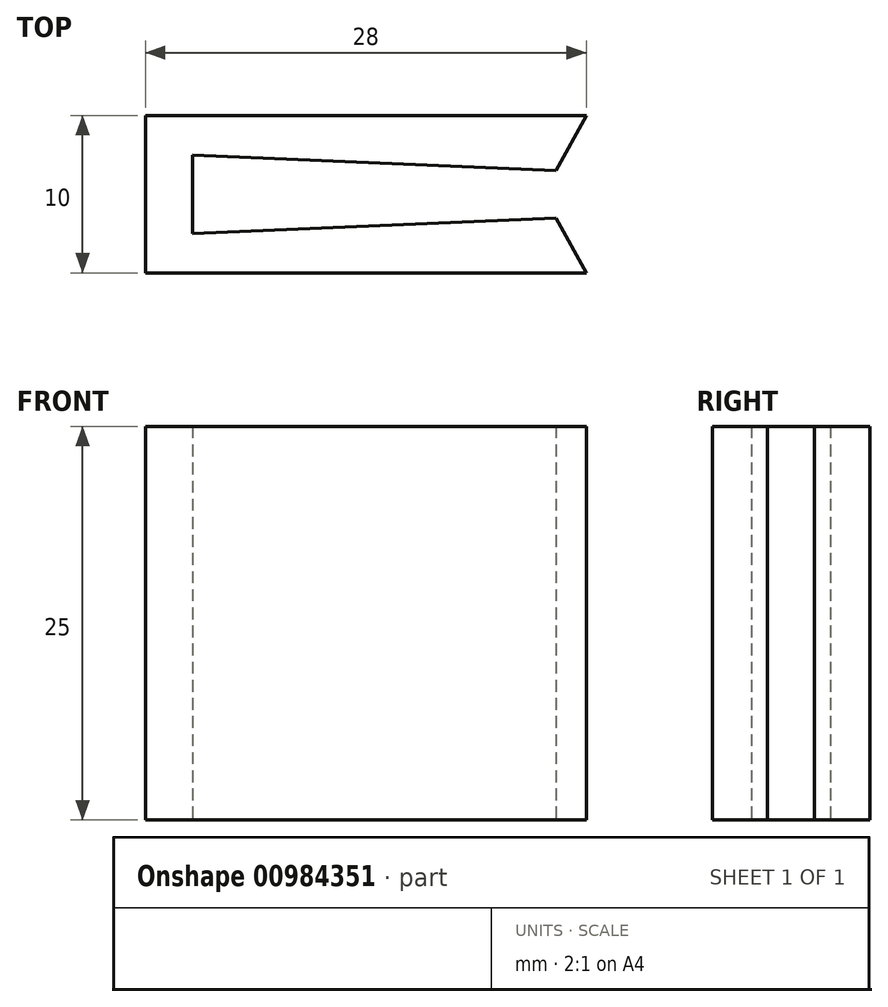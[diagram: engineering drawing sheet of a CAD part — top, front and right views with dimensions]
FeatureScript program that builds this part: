
annotation { "Feature Type Name" : "Feature", "Feature Type Description" : "" }
export const myFeature = defineFeature(function(context is Context, id is Id, definition is map)
    precondition{}
    {
        {
            var Q0;
            Q0=qCreatedBy(makeId("Top.planeOp"),FACE);
            var sketch = newSketch(context, id + "F0", { "sketchPlane" : qUnion([Q0])});
            skLineSegment(sketch, "E0", {"start": v(11.72, 6.5) * mm, "end": v(-16.28, 6.5) * mm});
            skLineSegment(sketch, "E1", {"start": v(-16.28, 6.5) * mm, "end": v(-16.28, -3.5) * mm});
            skLineSegment(sketch, "E2", {"start": v(-16.28, -3.5) * mm, "end": v(11.72, -3.5) * mm});
            skLineSegment(sketch, "E3", {"start": v(11.72, -3.5) * mm, "end": v(9.79, 0) * mm});
            skLineSegment(sketch, "E4", {"start": v(9.79, 0) * mm, "end": v(-13.28, -1) * mm});
            skLineSegment(sketch, "E5", {"start": v(-13.28, -1) * mm, "end": v(-13.28, 4) * mm});
            skLineSegment(sketch, "E6", {"start": v(-13.28, 4) * mm, "end": v(9.79, 3) * mm});
            skLineSegment(sketch, "E7", {"start": v(9.79, 3) * mm, "end": v(11.72, 6.5) * mm});
            skSolve(sketch);
        }
        {
            var Q0;
            Q0=makeQuery(id+"F0.imprint","IMPRINT",FACE,{"disambiguationData":[TD([[makeQuery(id+"F0.imprint","IMPRINT",EDGE,{"derivedFrom":sQuery(id+"F0.wireOp",EDGE,"E0")}),1.0]])]});
            extrude(context, id + "F1", {"entities" : qUnion([Q0]), "depth" : 25 * mm, "offsetDistance" : 25 * mm});
        }
    });
